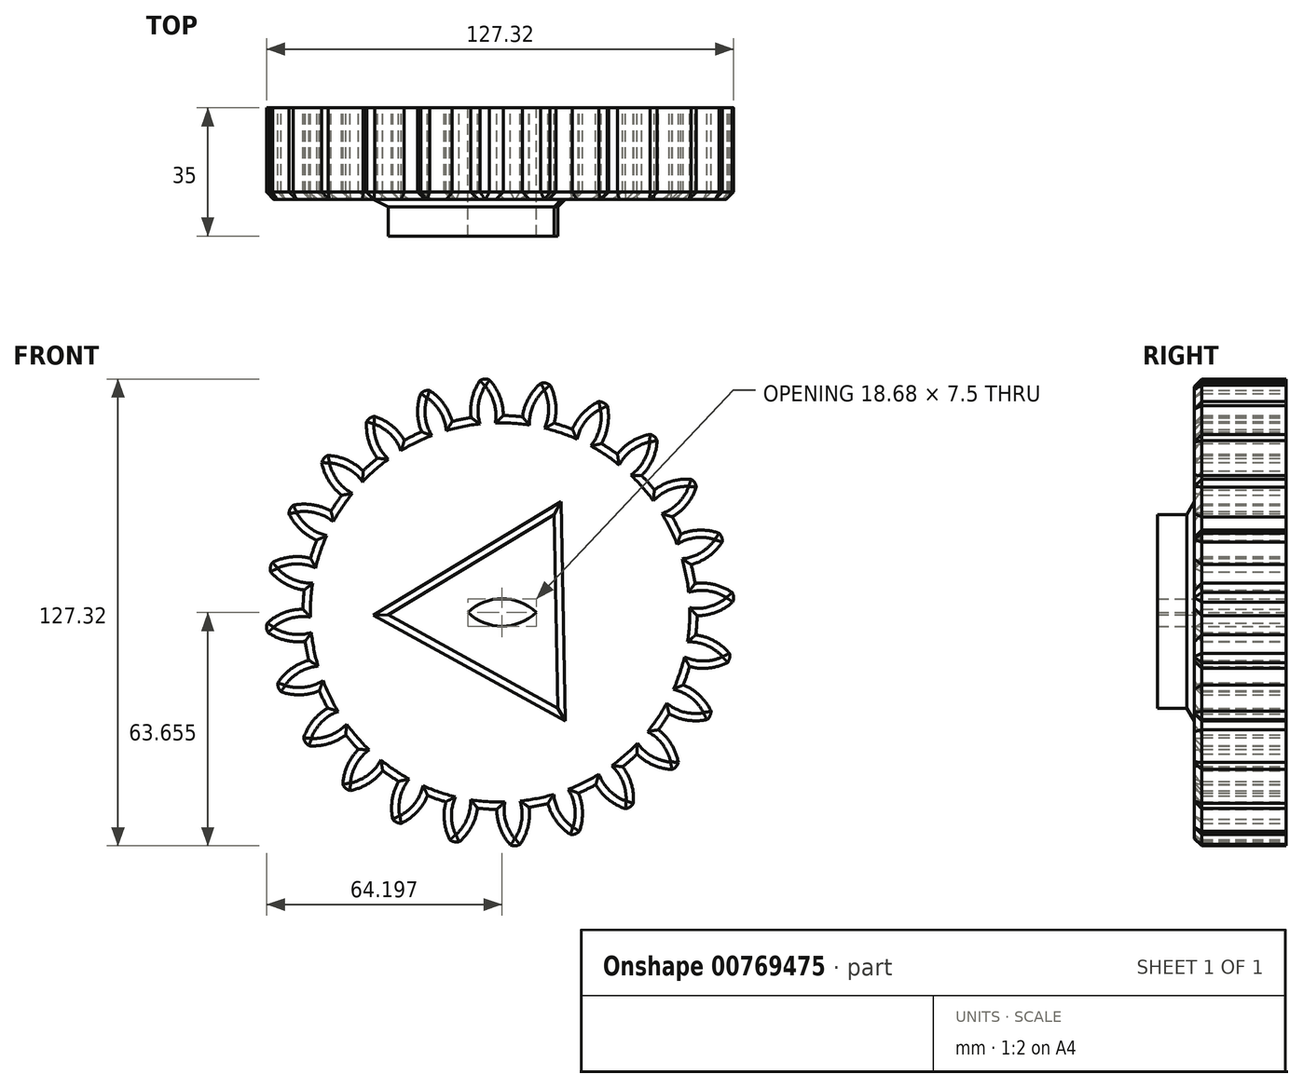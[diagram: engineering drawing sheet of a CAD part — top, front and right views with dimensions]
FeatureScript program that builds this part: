
annotation { "Feature Type Name" : "Feature", "Feature Type Description" : "" }
export const myFeature = defineFeature(function(context is Context, id is Id, definition is map)
    precondition{}
    {
        {
            var Q0;
            Q0=qCreatedBy(makeId("Front.planeOp"),FACE);
            var sketch = newSketch(context, id + "F0", { "sketchPlane" : qUnion([Q0])});
            skCircle(sketch, "E0", {"center": v(0, 0) * mm, "radius": 63.5 * mm, "construction": true});
            skCircle(sketch, "E1", {"center": v(0, 0) * mm, "radius": 58.67 * mm, "construction": true});
            skCircle(sketch, "E2", {"center": v(0, 0) * mm, "radius": 53.72 * mm});
            skLineSegment(sketch, "E3", {"start": v(0, 0) * mm, "end": v(0, 75.37) * mm, "construction": true});
            skLineSegment(sketch, "E4", {"start": v(0, 0) * mm, "end": v(-4.94, 75.37) * mm, "construction": true});
            skLineSegment(sketch, "E5", {"start": v(0, 58.67) * mm, "end": v(-55.05, 58.67) * mm, "construction": true});
            skLineSegment(sketch, "E6", {"start": v(0, 58.67) * mm, "end": v(-49.24, 40.75) * mm, "construction": true});
            skCircle(sketch, "E7", {"center": v(0, 0) * mm, "radius": 55.14 * mm, "construction": true});
            skCircle(sketch, "E8", {"center": v(0, 58.67) * mm, "radius": 14.6 * mm, "construction": true});
            skCircle(sketch, "E9", {"center": v(-13.72, 53.68) * mm, "radius": 14.6 * mm, "construction": true});
            skArc(sketch, "E10", {"start": v(0, 58.67) * mm, "mid": v(-1.2, 61.2) * mm, "end": v(-2.86, 63.44) * mm});
            skArc(sketch, "E11", {"start": v(0.88, 53.71) * mm, "mid": v(0.67, 56.23) * mm, "end": v(0, 58.67) * mm});
            skArc(sketch, "E12.MirrorCS", {"start": v(-7.66, 58.17) * mm, "mid": v(-6.8, 60.82) * mm, "end": v(-5.45, 63.27) * mm});
            skArc(sketch, "E13.MirrorCS", {"start": v(-7.88, 53.14) * mm, "mid": v(-8, 55.67) * mm, "end": v(-7.66, 58.17) * mm});
            skArc(sketch, "E14", {"start": v(-2.86, 63.44) * mm, "mid": v(-4.17, 63.66) * mm, "end": v(-5.45, 63.27) * mm});
            skCircle(sketch, "E15.cCircle", {"center": v(0, 0) * mm, "radius": 30.5 * mm, "construction": true});
            skLineSegment(sketch, "E15.0", {"start": v(15.78, -26.11) * mm, "end": v(-30.5, -0.61) * mm});
            skLineSegment(sketch, "E15.1", {"start": v(-30.5, -0.61) * mm, "end": v(14.72, 26.72) * mm});
            skLineSegment(sketch, "E15.2", {"start": v(14.72, 26.72) * mm, "end": v(15.78, -26.11) * mm});
            skArc(sketch, "E16", {"start": v(9.88, 0) * mm, "mid": v(0.54, 3.74) * mm, "end": v(-8.8, 0) * mm});
            skArc(sketch, "E17", {"start": v(-8.8, 0) * mm, "mid": v(0.54, -3.75) * mm, "end": v(9.88, 0) * mm});
            skSolve(sketch);
        }
        {
            var Q0;
            {var subQ0=sQuery(id+"F0.wireOp",EDGE,"E2");var subQ1=makeQuery(id+"F0.imprint","INTERSECT",VERTEX,{"derivedFrom":[subQ0,sQuery(id+"F0.wireOp",EDGE,"E11")]});Q0=makeQuery(id+"F0.imprint","IMPRINT",FACE,{"disambiguationData":[TD([[makeQuery(id+"F0.imprint","IMPRINT",EDGE,{"disambiguationData":[TD([[subQ1,-1.0]])],"derivedFrom":subQ0}),1.0]])]});}
            var Q1;
            Q1=makeQuery(id+"F0.imprint","IMPRINT",FACE,{"disambiguationData":[TD([[makeQuery(id+"F0.imprint","IMPRINT",EDGE,{"derivedFrom":sQuery(id+"F0.wireOp",EDGE,"E10")}),1.0]])]});
            extrude(context, id + "F1", {"entities" : qUnion([Q0, Q1]), "depth" : 25 * mm, "offsetDistance" : 25 * mm});
        }
        {
            var Q0;
            Q0=makeQuery(id+"F1.opExtrude","SWEPT_BODY",BODY,{"disambiguationData":[OSD([sQuery(id+"F0.wireOp",EDGE,"E2"),sQuery(id+"F0.wireOp",EDGE,"E10"),sQuery(id+"F0.wireOp",EDGE,"E11"),sQuery(id+"F0.wireOp",EDGE,"E12.MirrorCS"),sQuery(id+"F0.wireOp",EDGE,"E13.MirrorCS"),sQuery(id+"F0.wireOp",EDGE,"E14")])]});
            var Q1;
            Q1=makeQuery(id+"F1.opExtrude","SWEPT_FACE",FACE,{"disambiguationData":[OSD([sQuery(id+"F0.wireOp",EDGE,"E2")])]});
            circularPattern(context, id + "F2", {"entities" : qUnion([Q0]), "axis" : qUnion([Q1]), "angle" : 360 * degree, "instanceCount" : 24, "equalSpace" : true});
        }
        {
            var Q0;
            Q0=makeQuery(id+"F0.imprint","IMPRINT",FACE,{"disambiguationData":[TD([[makeQuery(id+"F0.imprint","IMPRINT",EDGE,{"derivedFrom":sQuery(id+"F0.wireOp",EDGE,"E15.0")}),-1.0]])]});
            extrude(context, id + "F3", {"entities" : qUnion([Q0]), "operationType" : NewBodyOperationType.ADD, "depth" : 35 * mm, "offsetDistance" : 25 * mm});
        }
        {
            var Q0;
            {var subQ0=makeQuery(id+"F1.opExtrude","CAP_FACE",FACE,{"disambiguationData":[OSD([sQuery(id+"F0.wireOp",EDGE,"E2"),sQuery(id+"F0.wireOp",EDGE,"E10"),sQuery(id+"F0.wireOp",EDGE,"E11"),sQuery(id+"F0.wireOp",EDGE,"E12.MirrorCS"),sQuery(id+"F0.wireOp",EDGE,"E13.MirrorCS"),sQuery(id+"F0.wireOp",EDGE,"E14"),sQuery(id+"F0.wireOp",EDGE,"E15.0"),sQuery(id+"F0.wireOp",EDGE,"E15.1"),sQuery(id+"F0.wireOp",EDGE,"E15.2")])],"isStart":false});Q0=makeQuery(id+"F3.boolean.opBoolean","MERGE",FACE,{"derivedFrom":[subQ0,makeQuery(id+"F2.opPattern","COPY",FACE,{"derivedFrom":subQ0,"instanceName":"1"}),makeQuery(id+"F2.opPattern","COPY",FACE,{"derivedFrom":subQ0,"instanceName":"2"}),makeQuery(id+"F2.opPattern","COPY",FACE,{"derivedFrom":subQ0,"instanceName":"3"}),makeQuery(id+"F2.opPattern","COPY",FACE,{"derivedFrom":subQ0,"instanceName":"4"}),makeQuery(id+"F2.opPattern","COPY",FACE,{"derivedFrom":subQ0,"instanceName":"5"}),makeQuery(id+"F2.opPattern","COPY",FACE,{"derivedFrom":subQ0,"instanceName":"6"}),makeQuery(id+"F2.opPattern","COPY",FACE,{"derivedFrom":subQ0,"instanceName":"7"}),makeQuery(id+"F2.opPattern","COPY",FACE,{"derivedFrom":subQ0,"instanceName":"8"}),makeQuery(id+"F2.opPattern","COPY",FACE,{"derivedFrom":subQ0,"instanceName":"9"}),makeQuery(id+"F2.opPattern","COPY",FACE,{"derivedFrom":subQ0,"instanceName":"10"}),makeQuery(id+"F2.opPattern","COPY",FACE,{"derivedFrom":subQ0,"instanceName":"11"}),makeQuery(id+"F2.opPattern","COPY",FACE,{"derivedFrom":subQ0,"instanceName":"12"}),makeQuery(id+"F2.opPattern","COPY",FACE,{"derivedFrom":subQ0,"instanceName":"13"}),makeQuery(id+"F2.opPattern","COPY",FACE,{"derivedFrom":subQ0,"instanceName":"14"}),makeQuery(id+"F2.opPattern","COPY",FACE,{"derivedFrom":subQ0,"instanceName":"15"}),makeQuery(id+"F2.opPattern","COPY",FACE,{"derivedFrom":subQ0,"instanceName":"16"}),makeQuery(id+"F2.opPattern","COPY",FACE,{"derivedFrom":subQ0,"instanceName":"17"}),makeQuery(id+"F2.opPattern","COPY",FACE,{"derivedFrom":subQ0,"instanceName":"18"}),makeQuery(id+"F2.opPattern","COPY",FACE,{"derivedFrom":subQ0,"instanceName":"19"}),makeQuery(id+"F2.opPattern","COPY",FACE,{"derivedFrom":subQ0,"instanceName":"20"}),makeQuery(id+"F2.opPattern","COPY",FACE,{"derivedFrom":subQ0,"instanceName":"21"}),makeQuery(id+"F2.opPattern","COPY",FACE,{"derivedFrom":subQ0,"instanceName":"22"}),makeQuery(id+"F2.opPattern","COPY",FACE,{"derivedFrom":subQ0,"instanceName":"23"})]});}
            chamfer(context, id + "F4", {"entities" : qUnion([Q0]), "width" : 2 * mm, "tangentPropagation" : true});
        }
    });
